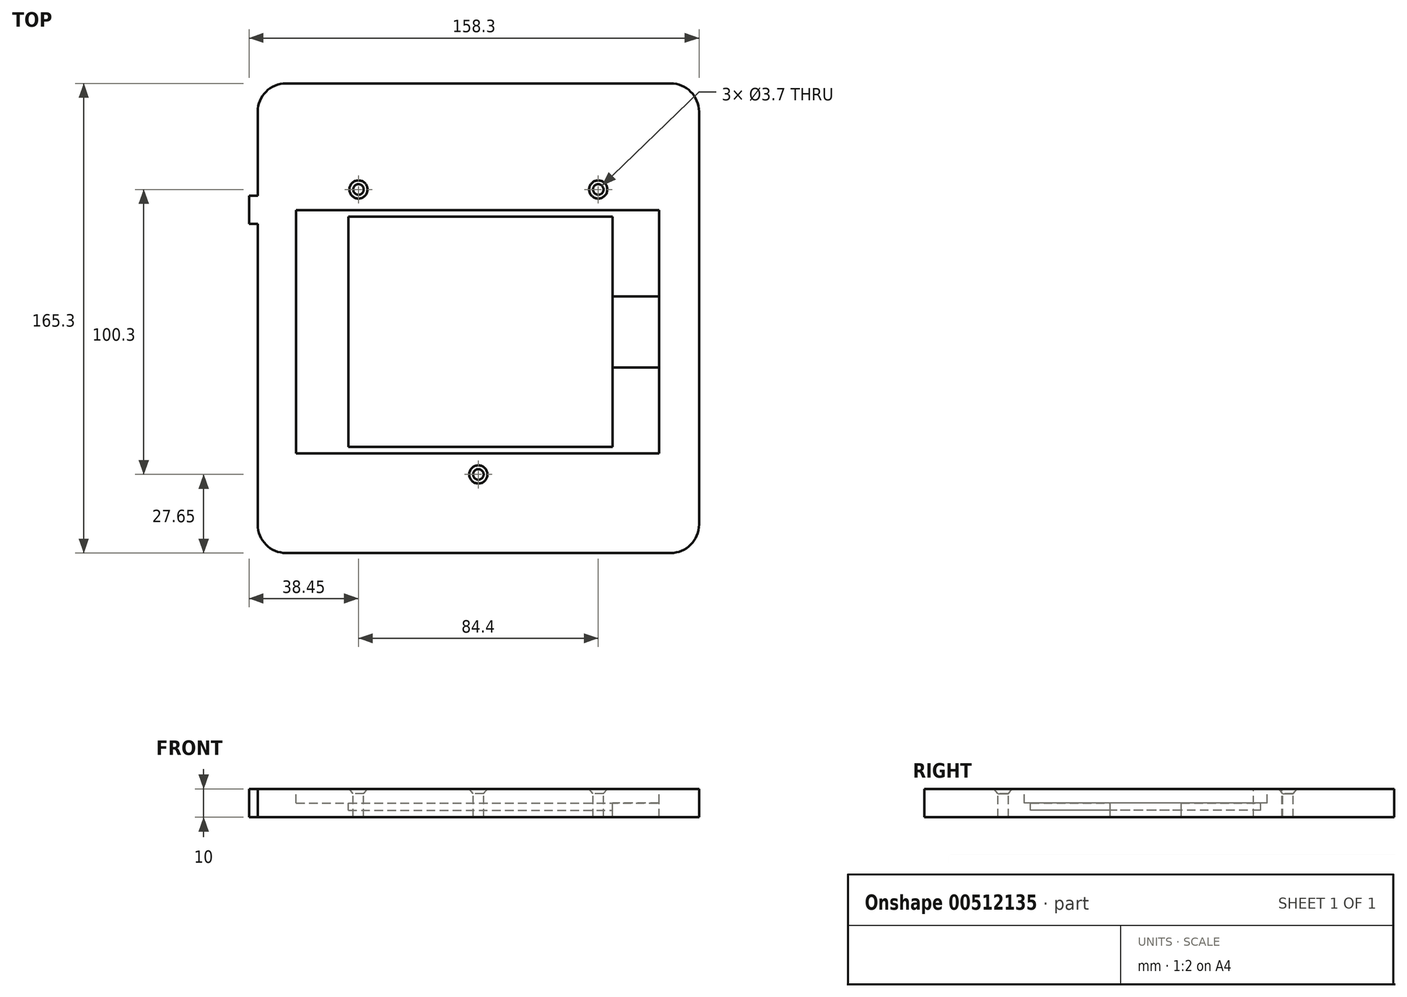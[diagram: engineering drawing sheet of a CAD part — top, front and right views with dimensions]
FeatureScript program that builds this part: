
annotation { "Feature Type Name" : "Feature", "Feature Type Description" : "" }
export const myFeature = defineFeature(function(context is Context, id is Id, definition is map)
    precondition{}
    {
        {
            assignVariable(context, id + "F0", {"name" : "s", "anyValue" : 10 * mm});
        }
        {
            var Q0;
            Q0=qCreatedBy(makeId("Top.planeOp"),FACE);
            cPlane(context, id + "F1", {"entities" : qUnion([Q0]), "cplaneType" : CPlaneType.OFFSET, "offset" : getVariable(context, 's'), "width" : 150 * mm, "height" : 150 * mm});
        }
        {
            var Q0;
            Q0=qCreatedBy(id+"F1.planeOp",FACE);
            var sketch = newSketch(context, id + "F2", { "sketchPlane" : qUnion([Q0])});
            skLineSegment(sketch, "E0.bottom", {"start": v(67.65, 82.65) * mm, "end": v(-67.65, 82.65) * mm});
            skLineSegment(sketch, "E0.top", {"start": v(67.65, -82.65) * mm, "end": v(-67.65, -82.65) * mm});
            skLineSegment(sketch, "E0.left", {"start": v(77.65, 72.65) * mm, "end": v(77.65, -72.65) * mm});
            skLineSegment(sketch, "E0.right", {"start": v(-77.65, 72.65) * mm, "end": v(-77.65, -72.65) * mm});
            skPoint(sketch, "E0.middle", {"position": v(0, 0) * mm});
            skPoint(sketch, "E1.visualSharp", {"position": v(-77.65, 82.65) * mm});
            skArc(sketch, "E1.filletArc", {"start": v(-67.65, 82.65) * mm, "mid": v(-74.72, 79.72) * mm, "end": v(-77.65, 72.65) * mm});
            skPoint(sketch, "E2.visualSharp", {"position": v(-77.65, -82.65) * mm});
            skArc(sketch, "E2.filletArc", {"start": v(-77.65, -72.65) * mm, "mid": v(-74.72, -79.72) * mm, "end": v(-67.65, -82.65) * mm});
            skPoint(sketch, "E3.visualSharp", {"position": v(77.65, -82.65) * mm});
            skArc(sketch, "E3.filletArc", {"start": v(67.65, -82.65) * mm, "mid": v(74.72, -79.72) * mm, "end": v(77.65, -72.65) * mm});
            skPoint(sketch, "E4.visualSharp", {"position": v(77.65, 82.65) * mm});
            skArc(sketch, "E4.filletArc", {"start": v(77.65, 72.65) * mm, "mid": v(74.72, 79.72) * mm, "end": v(67.65, 82.65) * mm});
            skCircle(sketch, "E5", {"center": v(42.2, 45.3) * mm, "radius": 1.85 * mm});
            skCircle(sketch, "E6", {"center": v(-42.2, 45.3) * mm, "radius": 1.85 * mm});
            skCircle(sketch, "E7", {"center": v(0, -55) * mm, "radius": 1.85 * mm});
            skLineSegment(sketch, "E8.bottom", {"start": v(-64.15, 37.95) * mm, "end": v(63.55, 37.95) * mm});
            skLineSegment(sketch, "E8.top", {"start": v(-64.15, -47.55) * mm, "end": v(63.55, -47.55) * mm});
            skLineSegment(sketch, "E8.left", {"start": v(-64.15, 37.95) * mm, "end": v(-64.15, -47.55) * mm});
            skLineSegment(sketch, "E8.right", {"start": v(63.55, 37.95) * mm, "end": v(63.55, -47.55) * mm});
            skLineSegment(sketch, "E9.bottom", {"start": v(63.55, 7.7) * mm, "end": v(47.2, 7.7) * mm});
            skLineSegment(sketch, "E9.top", {"start": v(63.55, -17.3) * mm, "end": v(47.2, -17.3) * mm});
            skLineSegment(sketch, "E9.left", {"start": v(63.55, 7.7) * mm, "end": v(63.55, -17.3) * mm});
            skLineSegment(sketch, "E9.right", {"start": v(47.2, 7.7) * mm, "end": v(47.2, -17.3) * mm});
            skLineSegment(sketch, "E10", {"start": v(47.2, 7.7) * mm, "end": v(47.2, 37.95) * mm, "construction": true});
            skLineSegment(sketch, "E11", {"start": v(47.2, -17.3) * mm, "end": v(47.2, -47.55) * mm, "construction": true});
            skLineSegment(sketch, "E12", {"start": v(-77.65, 82.65) * mm, "end": v(-77.65, 43.15) * mm, "construction": true});
            skLineSegment(sketch, "E13.bottom", {"start": v(-77.65, 43.15) * mm, "end": v(-80.65, 43.15) * mm});
            skLineSegment(sketch, "E13.top", {"start": v(-77.65, 33.15) * mm, "end": v(-80.65, 33.15) * mm});
            skLineSegment(sketch, "E13.left", {"start": v(-77.65, 43.15) * mm, "end": v(-77.65, 33.15) * mm});
            skLineSegment(sketch, "E13.right", {"start": v(-80.65, 43.15) * mm, "end": v(-80.65, 33.15) * mm});
            skLineSegment(sketch, "E14", {"start": v(-64.15, 37.95) * mm, "end": v(63.55, -47.55) * mm, "construction": true});
            skLineSegment(sketch, "E15", {"start": v(-64.15, -47.55) * mm, "end": v(63.55, 37.95) * mm, "construction": true});
            skPoint(sketch, "E16", {"position": v(-0.3, -4.8) * mm});
            skLineSegment(sketch, "E17.bottom", {"start": v(60.2, 35.7) * mm, "end": v(-60.8, 35.7) * mm, "construction": true});
            skLineSegment(sketch, "E17.top", {"start": v(60.2, -45.3) * mm, "end": v(-60.8, -45.3) * mm, "construction": true});
            skLineSegment(sketch, "E17.left", {"start": v(60.2, 35.7) * mm, "end": v(60.2, -45.3) * mm, "construction": true});
            skLineSegment(sketch, "E17.right", {"start": v(-60.8, 35.7) * mm, "end": v(-60.8, -45.3) * mm, "construction": true});
            skLineSegment(sketch, "E18", {"start": v(-45.8, 35.7) * mm, "end": v(47.2, 35.7) * mm});
            skLineSegment(sketch, "E19", {"start": v(-45.8, 35.7) * mm, "end": v(-45.8, -45.3) * mm});
            skLineSegment(sketch, "E20", {"start": v(-45.8, -45.3) * mm, "end": v(47.2, -45.3) * mm});
            skLineSegment(sketch, "E21", {"start": v(47.2, -45.3) * mm, "end": v(47.2, 35.7) * mm});
            skSolve(sketch);
        }
        {
            var Q0;
            Q0=makeQuery(id+"F2.imprint","IMPRINT",FACE,{"disambiguationData":[TD([[makeQuery(id+"F2.imprint","IMPRINT",EDGE,{"derivedFrom":sQuery(id+"F2.wireOp",EDGE,"E0.bottom")}),1.0]])]});
            var Q1;
            Q1=makeQuery(id+"F2.imprint","IMPRINT",FACE,{"disambiguationData":[TD([[makeQuery(id+"F2.imprint","IMPRINT",EDGE,{"derivedFrom":sQuery(id+"F2.wireOp",EDGE,"E8.bottom")}),-1.0]])]});
            var Q2;
            Q2=makeQuery(id+"F2.imprint","IMPRINT",FACE,{"disambiguationData":[TD([[makeQuery(id+"F2.imprint","IMPRINT",EDGE,{"derivedFrom":sQuery(id+"F2.wireOp",EDGE,"E13.bottom")}),1.0]])]});
            var Q3;
            Q3=makeQuery(id+"F2.imprint","IMPRINT",FACE,{"disambiguationData":[TD([[makeQuery(id+"F2.imprint","IMPRINT",EDGE,{"derivedFrom":sQuery(id+"F2.wireOp",EDGE,"E9.right")}),-1.0]])]});
            var Q4;
            {var subQ3=sQuery(id+"F2.wireOp",EDGE,"E18");Q4=makeQuery(id+"F2.imprint","IMPRINT",FACE,{"disambiguationData":[TD([[makeQuery(id+"F2.imprint","IMPRINT",EDGE,{"derivedFrom":subQ3}),-1.0]])]});}
            extrude(context, id + "F3", {"entities" : qUnion([Q0, Q1, Q2, Q3, Q4]), "oppositeDirection" : true, "depth" : getVariable(context, 's'), "offsetDistance" : 25 * mm});
        }
        {
            var Q0;
            Q0=makeQuery(id+"F2.imprint","IMPRINT",FACE,{"disambiguationData":[TD([[makeQuery(id+"F2.imprint","IMPRINT",EDGE,{"derivedFrom":sQuery(id+"F2.wireOp",EDGE,"E8.bottom")}),-1.0]])]});
            extrude(context, id + "F4", {"entities" : qUnion([Q0]), "operationType" : NewBodyOperationType.REMOVE, "oppositeDirection" : true, "depth" : 5 * mm, "offsetDistance" : 25 * mm});
        }
        {
            var Q0;
            {var subQ3=sQuery(id+"F2.wireOp",EDGE,"E18");Q0=makeQuery(id+"F2.imprint","IMPRINT",FACE,{"disambiguationData":[TD([[makeQuery(id+"F2.imprint","IMPRINT",EDGE,{"derivedFrom":subQ3}),-1.0]])]});}
            extrude(context, id + "F5", {"entities" : qUnion([Q0]), "operationType" : NewBodyOperationType.REMOVE, "oppositeDirection" : true, "depth" : 7.5 * mm, "offsetDistance" : 25 * mm});
        }
        {
            var Q0;
            Q0=sQuery(id+"F2.wireOp",VERTEX,"E6.center");
            var Q1;
            Q1=sQuery(id+"F2.wireOp",VERTEX,"E5.center");
            var Q2;
            Q2=sQuery(id+"F2.wireOp",VERTEX,"E7.center");
            var Q3;
            Q3=makeQuery(id+"F3.opExtrude","SWEPT_BODY",BODY,{"disambiguationData":[OSD([sQuery(id+"F2.wireOp",EDGE,"E0.bottom"),sQuery(id+"F2.wireOp",EDGE,"E0.top"),sQuery(id+"F2.wireOp",EDGE,"E0.left"),sQuery(id+"F2.wireOp",EDGE,"E0.right"),sQuery(id+"F2.wireOp",EDGE,"E1.filletArc"),sQuery(id+"F2.wireOp",EDGE,"E2.filletArc"),sQuery(id+"F2.wireOp",EDGE,"E3.filletArc"),sQuery(id+"F2.wireOp",EDGE,"E4.filletArc")])]});
            hole(context, id + "F6", {"style" : HoleStyle.C_SINK, "endStyle" : HoleEndStyle.THROUGH, "holeDiameter" : 3.7 * mm, "cSinkDiameter" : 6.4 * mm, "cSinkAngle" : 78 * degree, "isTappedThrough" : true, "tappedDepth" : 12 * mm, "tapClearance" : 3, "locations" : qUnion([Q0, Q1, Q2]), "scope" : qUnion([Q3])});
        }
    });
